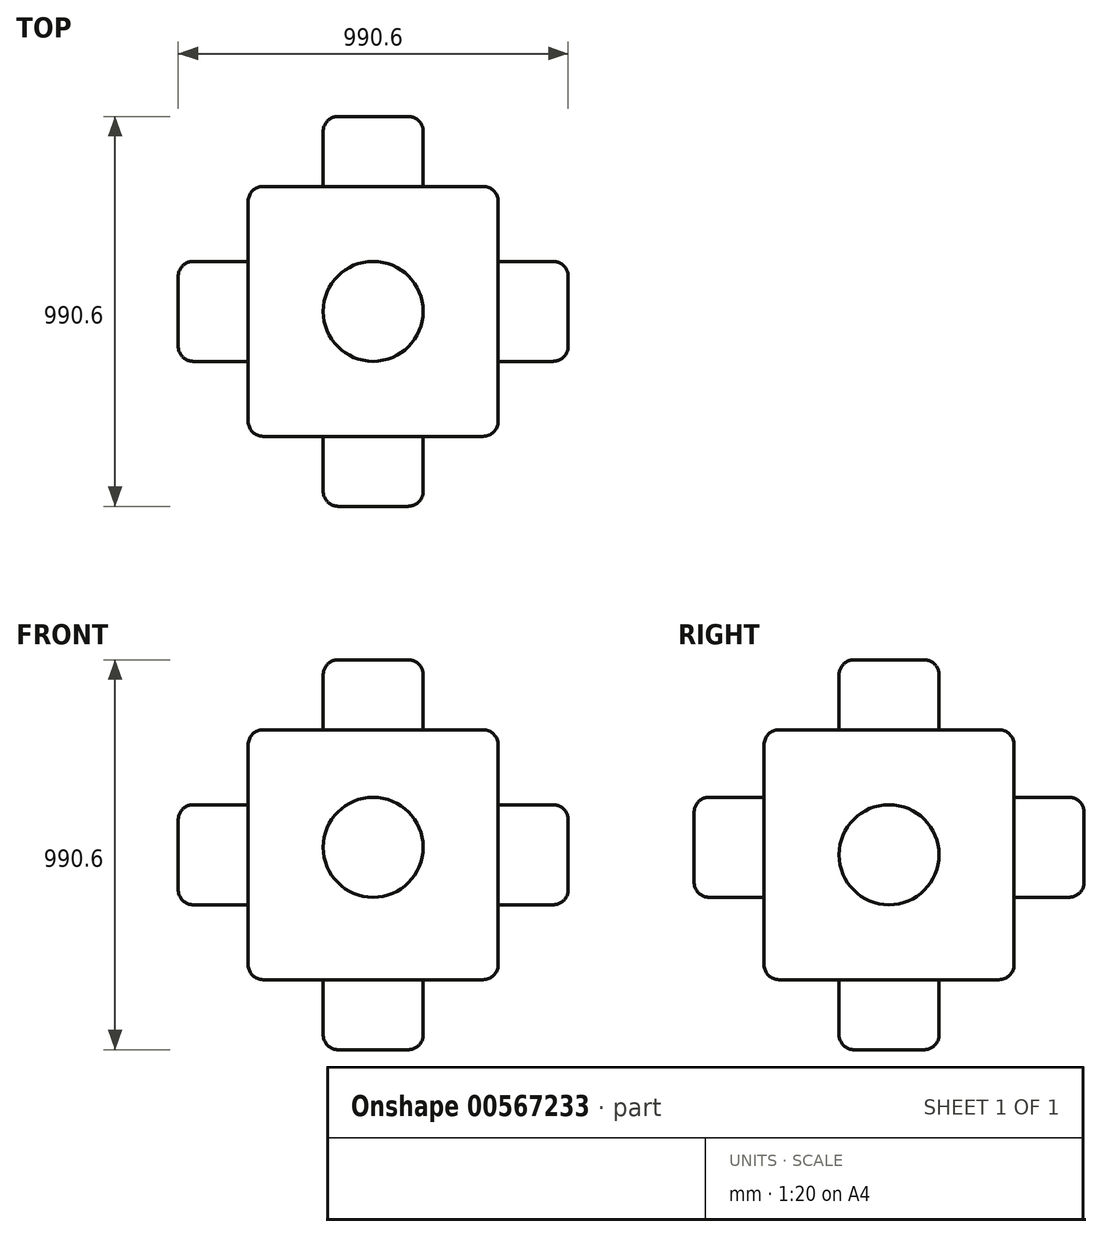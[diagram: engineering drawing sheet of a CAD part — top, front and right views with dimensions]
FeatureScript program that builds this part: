
annotation { "Feature Type Name" : "Feature", "Feature Type Description" : "" }
export const myFeature = defineFeature(function(context is Context, id is Id, definition is map)
    precondition{}
    {
        {
            var Q0;
            Q0=qCreatedBy(makeId("Front.planeOp"),FACE);
            var sketch = newSketch(context, id + "F0", { "sketchPlane" : qUnion([Q0])});
            skLineSegment(sketch, "E0.bottom", {"start": v(-317.5, 317.5) * mm, "end": v(317.5, 317.5) * mm});
            skLineSegment(sketch, "E0.top", {"start": v(-317.5, -317.5) * mm, "end": v(317.5, -317.5) * mm});
            skLineSegment(sketch, "E0.left", {"start": v(-317.5, 317.5) * mm, "end": v(-317.5, -317.5) * mm});
            skLineSegment(sketch, "E0.right", {"start": v(317.5, 317.5) * mm, "end": v(317.5, -317.5) * mm});
            skCircle(sketch, "E1", {"center": v(0, 18.89) * mm, "radius": 127 * mm});
            skSolve(sketch);
        }
        {
            var Q0;
            Q0=makeQuery(id+"F0.imprint","IMPRINT",FACE,{"disambiguationData":[TD([[makeQuery(id+"F0.imprint","IMPRINT",EDGE,{"derivedFrom":sQuery(id+"F0.wireOp",EDGE,"E1")}),1.0]])]});
            extrude(context, id + "F1", {"entities" : qUnion([Q0]), "depth" : 177.8 * mm, "offsetDistance" : 25.4 * mm, "hasSecondDirection" : true, "secondDirectionOppositeDirection" : true, "secondDirectionDepth" : 812.8 * mm});
        }
        {
            var Q0;
            Q0=makeQuery(id+"F0.imprint","IMPRINT",FACE,{"disambiguationData":[TD([[makeQuery(id+"F0.imprint","IMPRINT",EDGE,{"derivedFrom":sQuery(id+"F0.wireOp",EDGE,"E0.bottom")}),-1.0]])]});
            extrude(context, id + "F2", {"entities" : qUnion([Q0]), "operationType" : NewBodyOperationType.ADD, "oppositeDirection" : true, "depth" : 635 * mm, "offsetDistance" : 25.4 * mm});
        }
        {
            var Q0;
            Q0=makeQuery(id+"F2.opExtrude","SWEPT_EDGE",EDGE,{"disambiguationData":[OSD([sQuery(id+"F0.wireOp",EDGE,"E0.top"),sQuery(id+"F0.wireOp",EDGE,"E0.right")])]});
            var Q1;
            Q1=makeQuery(id+"F2.opExtrude","SWEPT_EDGE",EDGE,{"disambiguationData":[OSD([sQuery(id+"F0.wireOp",EDGE,"E0.bottom"),sQuery(id+"F0.wireOp",EDGE,"E0.right")])]});
            var Q2;
            Q2=makeQuery(id+"F2.opExtrude","SWEPT_EDGE",EDGE,{"disambiguationData":[OSD([sQuery(id+"F0.wireOp",EDGE,"E0.bottom"),sQuery(id+"F0.wireOp",EDGE,"E0.left")])]});
            var Q3;
            Q3=makeQuery(id+"F2.opExtrude","CAP_EDGE",EDGE,{"disambiguationData":[OSD([sQuery(id+"F0.wireOp",EDGE,"E0.bottom")])],"isStart":false});
            var Q4;
            Q4=makeQuery(id+"F2.opExtrude","CAP_EDGE",EDGE,{"disambiguationData":[OSD([sQuery(id+"F0.wireOp",EDGE,"E0.left")])],"isStart":false});
            var Q5;
            Q5=makeQuery(id+"F2.opExtrude","CAP_EDGE",EDGE,{"disambiguationData":[OSD([sQuery(id+"F0.wireOp",EDGE,"E0.right")])],"isStart":false});
            var Q6;
            Q6=makeQuery(id+"F2.opExtrude","CAP_EDGE",EDGE,{"disambiguationData":[OSD([sQuery(id+"F0.wireOp",EDGE,"E0.top")])],"isStart":false});
            var Q7;
            Q7=makeQuery(id+"F2.opExtrude","SWEPT_EDGE",EDGE,{"disambiguationData":[OSD([sQuery(id+"F0.wireOp",EDGE,"E0.top"),sQuery(id+"F0.wireOp",EDGE,"E0.left")])]});
            var Q8;
            Q8=makeQuery(id+"F2.opExtrude","CAP_EDGE",EDGE,{"disambiguationData":[OSD([sQuery(id+"F0.wireOp",EDGE,"E0.left")])],"isStart":true});
            var Q9;
            Q9=makeQuery(id+"F2.opExtrude","CAP_EDGE",EDGE,{"disambiguationData":[OSD([sQuery(id+"F0.wireOp",EDGE,"E0.bottom")])],"isStart":true});
            var Q10;
            Q10=makeQuery(id+"F2.opExtrude","CAP_EDGE",EDGE,{"disambiguationData":[OSD([sQuery(id+"F0.wireOp",EDGE,"E0.right")])],"isStart":true});
            var Q11;
            Q11=makeQuery(id+"F2.opExtrude","CAP_EDGE",EDGE,{"disambiguationData":[OSD([sQuery(id+"F0.wireOp",EDGE,"E0.top")])],"isStart":true});
            fillet(context, id + "F3", {"entities" : qUnion([Q0, Q1, Q2, Q3, Q4, Q5, Q6, Q7, Q8, Q9, Q10, Q11]), "radius" : 38.1 * mm, "tangentPropagation" : true, "allowEdgeOverflow" : false});
        }
        {
            var Q0;
            Q0=makeQuery(id+"F2.opExtrude","SWEPT_FACE",FACE,{"disambiguationData":[OSD([sQuery(id+"F0.wireOp",EDGE,"E0.bottom")])]});
            var sketch = newSketch(context, id + "F4", { "sketchPlane" : qUnion([Q0])});
            skCircle(sketch, "E2", {"center": v(0, 317.5) * mm, "radius": 127 * mm});
            skSolve(sketch);
        }
        {
            var Q0;
            Q0=makeQuery(id+"F4.imprint","IMPRINT",FACE,{"disambiguationData":[TD([[makeQuery(id+"F4.imprint","IMPRINT",EDGE,{"derivedFrom":sQuery(id+"F4.wireOp",EDGE,"E2")}),1.0]])]});
            extrude(context, id + "F5", {"entities" : qUnion([Q0]), "operationType" : NewBodyOperationType.ADD, "depth" : 177.8 * mm, "offsetDistance" : 25.4 * mm, "hasSecondDirection" : true, "secondDirectionOppositeDirection" : true, "secondDirectionDepth" : 812.8 * mm});
        }
        {
            var Q0;
            Q0=makeQuery(id+"F2.opExtrude","SWEPT_FACE",FACE,{"disambiguationData":[OSD([sQuery(id+"F0.wireOp",EDGE,"E0.right")])]});
            var sketch = newSketch(context, id + "F6", { "sketchPlane" : qUnion([Q0])});
            skCircle(sketch, "E3", {"center": v(317.5, 0) * mm, "radius": 127 * mm});
            skSolve(sketch);
        }
        {
            var Q0;
            Q0=makeQuery(id+"F6.imprint","IMPRINT",FACE,{"disambiguationData":[TD([[makeQuery(id+"F6.imprint","IMPRINT",EDGE,{"derivedFrom":sQuery(id+"F6.wireOp",EDGE,"E3")}),1.0]])]});
            extrude(context, id + "F7", {"entities" : qUnion([Q0]), "operationType" : NewBodyOperationType.ADD, "depth" : 177.8 * mm, "offsetDistance" : 25.4 * mm, "hasSecondDirection" : true, "secondDirectionOppositeDirection" : true, "secondDirectionDepth" : 812.8 * mm});
        }
        {
            var Q0;
            Q0=makeQuery(id+"F1.opExtrude","CAP_EDGE",EDGE,{"disambiguationData":[OSD([sQuery(id+"F0.wireOp",EDGE,"E1")])],"isStart":true});
            var Q1;
            Q1=makeQuery(id+"F7.opExtrude","CAP_EDGE",EDGE,{"disambiguationData":[OSD([sQuery(id+"F6.wireOp",EDGE,"E3")])],"isStart":false});
            var Q2;
            Q2=makeQuery(id+"F5.opExtrude","CAP_EDGE",EDGE,{"disambiguationData":[OSD([sQuery(id+"F4.wireOp",EDGE,"E2")])],"isStart":false});
            var Q3;
            Q3=makeQuery(id+"F7.opExtrude","CAP_EDGE",EDGE,{"disambiguationData":[OSD([sQuery(id+"F6.wireOp",EDGE,"E3")])],"isStart":true});
            var Q4;
            Q4=makeQuery(id+"F1.opExtrude","CAP_EDGE",EDGE,{"disambiguationData":[OSD([sQuery(id+"F0.wireOp",EDGE,"E1")])],"isStart":false});
            var Q5;
            Q5=makeQuery(id+"F5.opExtrude","CAP_EDGE",EDGE,{"disambiguationData":[OSD([sQuery(id+"F4.wireOp",EDGE,"E2")])],"isStart":true});
            fillet(context, id + "F8", {"entities" : qUnion([Q0, Q1, Q2, Q3, Q4, Q5]), "radius" : 38.1 * mm, "tangentPropagation" : true, "allowEdgeOverflow" : false});
        }
    });
